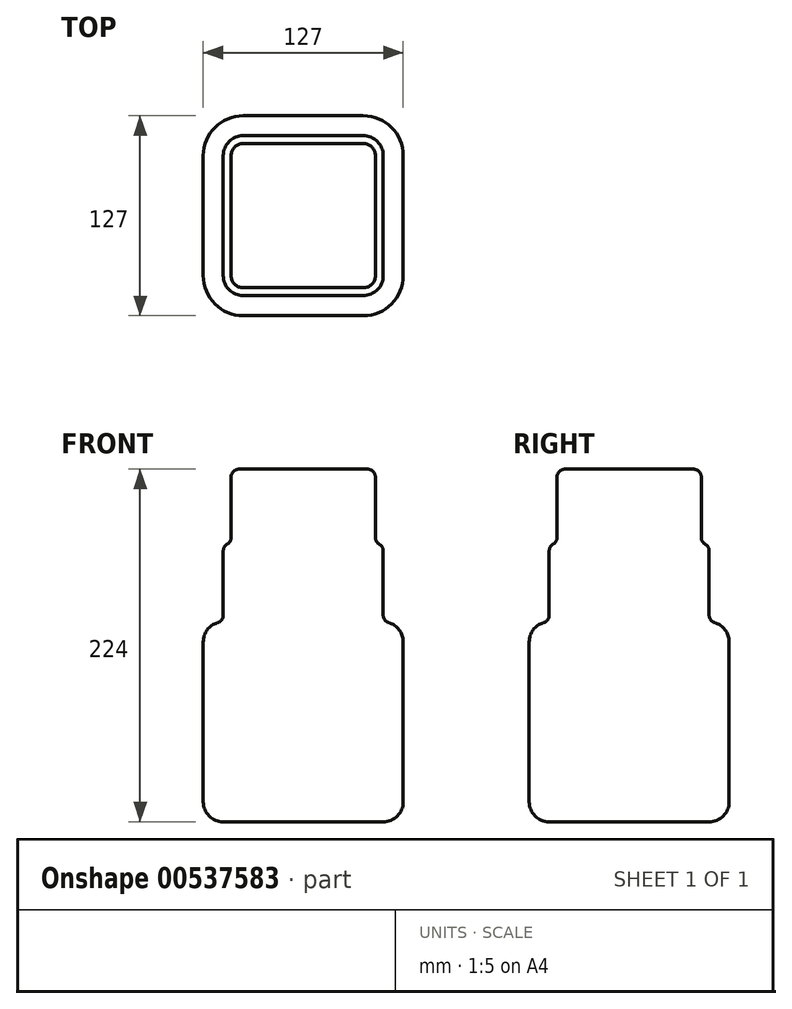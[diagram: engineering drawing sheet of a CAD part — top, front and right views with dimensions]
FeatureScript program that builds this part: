
annotation { "Feature Type Name" : "Feature", "Feature Type Description" : "" }
export const myFeature = defineFeature(function(context is Context, id is Id, definition is map)
    precondition{}
    {
        {
            var Q0;
            Q0=qCreatedBy(makeId("Front.planeOp"),FACE);
            var sketch = newSketch(context, id + "F0", { "sketchPlane" : qUnion([Q0])});
            skLineSegment(sketch, "E0.bottom", {"start": v(-63.5, 63.5) * mm, "end": v(63.5, 63.5) * mm});
            skLineSegment(sketch, "E0.top", {"start": v(-63.5, -63.5) * mm, "end": v(63.5, -63.5) * mm});
            skLineSegment(sketch, "E0.left", {"start": v(-63.5, 63.5) * mm, "end": v(-63.5, -63.5) * mm});
            skLineSegment(sketch, "E0.right", {"start": v(63.5, 63.5) * mm, "end": v(63.5, -63.5) * mm});
            skSolve(sketch);
        }
        {
            var Q0;
            Q0=makeQuery(id+"F0.imprint","IMPRINT",FACE,{"disambiguationData":[TD([[makeQuery(id+"F0.imprint","IMPRINT",EDGE,{"derivedFrom":sQuery(id+"F0.wireOp",EDGE,"E0.bottom")}),-1.0]])]});
            extrude(context, id + "F1", {"entities" : qUnion([Q0]), "depth" : 127 * mm, "offsetDistance" : 25.4 * mm});
        }
        {
            var Q0;
            Q0=makeQuery(id+"F1.opExtrude","CAP_EDGE",EDGE,{"disambiguationData":[OSD([sQuery(id+"F0.wireOp",EDGE,"E0.left")])],"isStart":false});
            var Q1;
            Q1=makeQuery(id+"F1.opExtrude","CAP_EDGE",EDGE,{"disambiguationData":[OSD([sQuery(id+"F0.wireOp",EDGE,"E0.right")])],"isStart":false});
            var Q2;
            Q2=makeQuery(id+"F1.opExtrude","CAP_EDGE",EDGE,{"disambiguationData":[OSD([sQuery(id+"F0.wireOp",EDGE,"E0.left")])],"isStart":true});
            var Q3;
            Q3=makeQuery(id+"F1.opExtrude","CAP_EDGE",EDGE,{"disambiguationData":[OSD([sQuery(id+"F0.wireOp",EDGE,"E0.right")])],"isStart":true});
            fillet(context, id + "F2", {"entities" : qUnion([Q0, Q1, Q2, Q3]), "radius" : 25.4 * mm, "tangentPropagation" : true, "allowEdgeOverflow" : false});
        }
        {
            var Q0;
            Q0=makeQuery(id+"F1.opExtrude","SWEPT_EDGE",EDGE,{"disambiguationData":[OSD([sQuery(id+"F0.wireOp",EDGE,"E0.bottom"),sQuery(id+"F0.wireOp",EDGE,"E0.left")])]});
            var Q1;
            Q1=makeQuery(id+"F1.opExtrude","CAP_EDGE",EDGE,{"disambiguationData":[OSD([sQuery(id+"F0.wireOp",EDGE,"E0.top")])],"isStart":false});
            fillet(context, id + "F3", {"entities" : qUnion([Q0, Q1]), "radius" : 12.7 * mm, "tangentPropagation" : true, "allowEdgeOverflow" : false});
        }
        {
            var Q0;
            Q0=makeQuery(id+"F1.opExtrude","SWEPT_FACE",FACE,{"disambiguationData":[OSD([sQuery(id+"F0.wireOp",EDGE,"E0.bottom")])]});
            extrude(context, id + "F4", {"entities" : qUnion([Q0]), "operationType" : NewBodyOperationType.ADD, "depth" : 50 * mm, "offsetDistance" : 25 * mm});
        }
        {
            var Q0;
            {var subQ0=sQuery(id+"F0.wireOp",EDGE,"E0.bottom");var subQ1=sQuery(id+"F0.wireOp",EDGE,"E0.left");Q0=makeQuery(id+"F4.opExtrude","CAP_EDGE",EDGE,{"disambiguationData":[OSD([subQ0,subQ1]),TDD([makeQuery(id+"F3.opFillet","BLEND_EDGE",EDGE,{"blendedFrom":[makeQuery(id+"F1.opExtrude","SWEPT_EDGE",EDGE,{"disambiguationData":[OSD([subQ0,subQ1])]}),makeQuery(id+"F1.opExtrude","SWEPT_FACE",FACE,{"disambiguationData":[OSD([subQ0])]})],"blendedInto":[makeQuery(id+"F1.opExtrude","SWEPT_FACE",FACE,{"disambiguationData":[OSD([subQ0])]})]})])],"isStart":false});}
            fillet(context, id + "F5", {"entities" : qUnion([Q0]), "radius" : 5 * mm, "tangentPropagation" : true, "allowEdgeOverflow" : false});
        }
        {
            var Q0;
            Q0=makeQuery(id+"F4.opExtrude","CAP_FACE",FACE,{"disambiguationData":[OSD([sQuery(id+"F0.wireOp",EDGE,"E0.bottom")])],"isStart":false});
            extrude(context, id + "F6", {"entities" : qUnion([Q0]), "operationType" : NewBodyOperationType.ADD, "depth" : 47 * mm, "offsetDistance" : 25 * mm});
        }
        {
            var Q0;
            {var subQ0=sQuery(id+"F0.wireOp",EDGE,"E0.bottom");var subQ1=sQuery(id+"F0.wireOp",EDGE,"E0.left");Q0=makeQuery(id+"F6.opExtrude","CAP_EDGE",EDGE,{"disambiguationData":[OSD([subQ0,subQ1]),TDD([makeQuery(id+"F5.opFillet","BLEND_EDGE",EDGE,{"blendedFrom":[makeQuery(id+"F4.opExtrude","CAP_EDGE",EDGE,{"disambiguationData":[OSD([subQ0,subQ1]),TDD([makeQuery(id+"F3.opFillet","BLEND_EDGE",EDGE,{"blendedFrom":[makeQuery(id+"F1.opExtrude","SWEPT_EDGE",EDGE,{"disambiguationData":[OSD([subQ0,subQ1])]}),makeQuery(id+"F1.opExtrude","SWEPT_FACE",FACE,{"disambiguationData":[OSD([subQ0])]})],"blendedInto":[makeQuery(id+"F1.opExtrude","SWEPT_FACE",FACE,{"disambiguationData":[OSD([subQ0])]})]})])],"isStart":false}),makeQuery(id+"F4.opExtrude","CAP_FACE",FACE,{"disambiguationData":[OSD([subQ0])],"isStart":false})],"blendedInto":[makeQuery(id+"F4.opExtrude","CAP_FACE",FACE,{"disambiguationData":[OSD([subQ0])],"isStart":false})]})])],"isStart":false});}
            fillet(context, id + "F7", {"entities" : qUnion([Q0]), "radius" : 5 * mm, "tangentPropagation" : true, "allowEdgeOverflow" : false});
        }
        {
            var Q0;
            {var subQ0=sQuery(id+"F0.wireOp",EDGE,"E0.bottom");var subQ1=makeQuery(id+"F5.opFillet","BLEND_EDGE",EDGE,{"blendedFrom":[makeQuery(id+"F4.opExtrude","CAP_EDGE",EDGE,{"disambiguationData":[OSD([subQ0]),TDD([makeQuery(id+"F3.opFillet","BLEND_EDGE",EDGE,{"blendedFrom":[makeQuery(id+"F1.opExtrude","CAP_EDGE",EDGE,{"disambiguationData":[OSD([subQ0])],"isStart":false}),makeQuery(id+"F1.opExtrude","SWEPT_FACE",FACE,{"disambiguationData":[OSD([subQ0])]})],"blendedInto":[makeQuery(id+"F1.opExtrude","SWEPT_FACE",FACE,{"disambiguationData":[OSD([subQ0])]})]})])],"isStart":false}),makeQuery(id+"F4.opExtrude","CAP_FACE",FACE,{"disambiguationData":[OSD([subQ0])],"isStart":false})],"blendedInto":[makeQuery(id+"F4.opExtrude","CAP_FACE",FACE,{"disambiguationData":[OSD([subQ0])],"isStart":false})]});Q0=makeQuery(id+"F6.boolean.opBoolean","MERGE",EDGE,{"derivedFrom":[subQ1,makeQuery(id+"F6.opExtrude","CAP_EDGE",EDGE,{"disambiguationData":[OSD([subQ0]),TDD([subQ1])],"isStart":true})]});}
            var Q1;
            {var subQ0=sQuery(id+"F0.wireOp",EDGE,"E0.bottom");var subQ1=makeQuery(id+"F3.opFillet","BLEND_EDGE",EDGE,{"blendedFrom":[makeQuery(id+"F1.opExtrude","CAP_EDGE",EDGE,{"disambiguationData":[OSD([subQ0])],"isStart":false}),makeQuery(id+"F1.opExtrude","SWEPT_FACE",FACE,{"disambiguationData":[OSD([subQ0])]})],"blendedInto":[makeQuery(id+"F1.opExtrude","SWEPT_FACE",FACE,{"disambiguationData":[OSD([subQ0])]})]});Q1=makeQuery(id+"F4.boolean.opBoolean","MERGE",EDGE,{"derivedFrom":[subQ1,makeQuery(id+"F4.opExtrude","CAP_EDGE",EDGE,{"disambiguationData":[OSD([subQ0]),TDD([subQ1])],"isStart":true})]});}
            fillet(context, id + "F8", {"entities" : qUnion([Q0, Q1]), "radius" : 5 * mm, "tangentPropagation" : true, "allowEdgeOverflow" : false});
        }
    });
